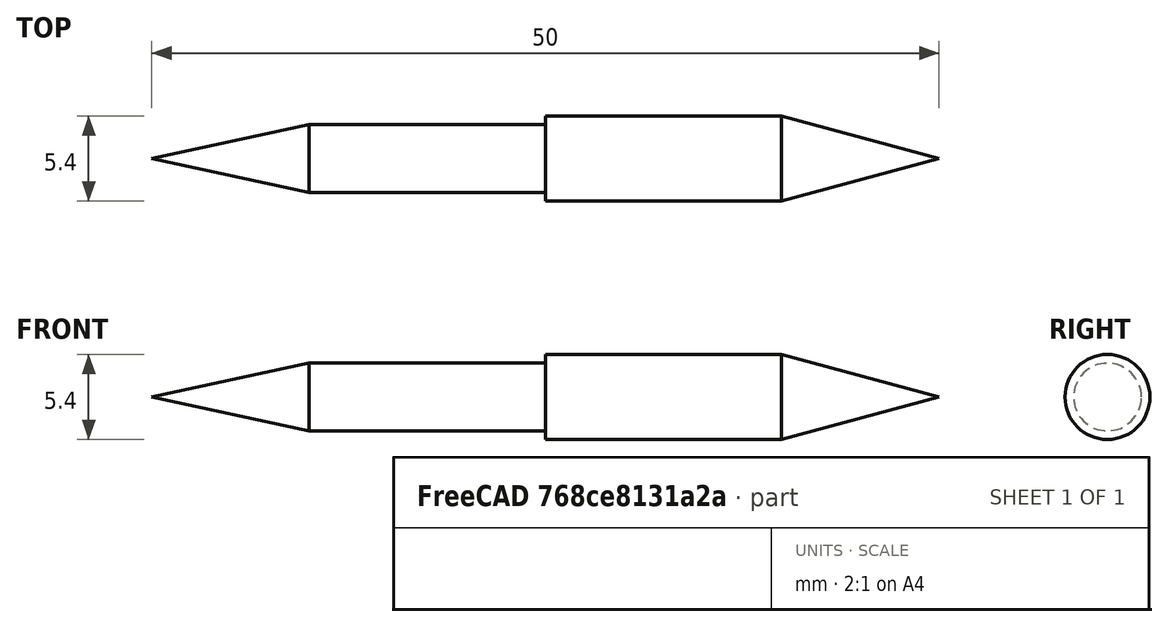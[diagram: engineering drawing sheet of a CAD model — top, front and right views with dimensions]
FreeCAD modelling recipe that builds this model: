
FCSTD DOCUMENT  (FreeCAD 1.0R38806 (Git))
Label: dowelpin
License: All rights reserved
LicenseURL: https://en.wikipedia.org/wiki/All_rights_reserved
objects: Sketcher::SketchObject×1, PartDesign::Revolution×1, PartDesign::Body×1
note: 6 computed .brp shape members not serialized (recipe doc carries the construction recipe); baked Part::Feature solids carry a one-line shape summary decoded from their .brp

FEATURE [Sketcher::SketchObject] Sketch
  ArcFitTolerance = 1e-06
  AttachmentSupport = -> [XZ_Plane]
  FullyConstrained = true
  MakeInternals = false
  MapMode = 5
  Placement = pos=(0,0,0) rot=(1,0,0;1.5708rad)
  sketch-geometry (6):
    g0: LineSegment StartX=-15 StartY=2.15 StartZ=0 EndX=0 EndY=2.15 EndZ=0
    g1: LineSegment StartX=0 StartY=2.7 StartZ=0 EndX=15 EndY=2.7 EndZ=0
    g2: LineSegment StartX=15 StartY=2.7 StartZ=0 EndX=25 EndY=0 EndZ=0
    g3: LineSegment StartX=-25 StartY=0 StartZ=0 EndX=-15 EndY=2.15 EndZ=0
    g4: LineSegment StartX=0 StartY=2.7 StartZ=0 EndX=0 EndY=2.15 EndZ=0
    g5: LineSegment StartX=-25 StartY=0 StartZ=0 EndX=25 EndY=0 EndZ=0
  constraints (18):
    c: Horizontal(g0)
    c: PointOnObject(g1,g-2)
    c: Horizontal(g1)
    c: Coincident(g2,g1)
    c: Coincident(g3,g0)
    c: Coincident(g4,g1)
    c: Coincident(g4,g0)
    c: DistanceX(g1,g1) = 15
    c: Coincident(g5,g3)
    c: PointOnObject(g5,g-1)
    c: Horizontal(g5)
    c: Distance(g5,g0) = 2.15
    c: Distance(g5,g1) = 2.7
    c: DistanceX(g0,g0) = 15
    c: PointOnObject(g0,g-2)
    c: Coincident(g5,g2)
    c: DistanceX(g3,g0) = 10
    c: DistanceX(g1,g2) = 10
FEATURE [PartDesign::Revolution] Revolution
  Angle = 360
  Angle2 = 60
  Axis = (1,0,0)
  Base = (0,0,0)
  Placement = pos=(0,0,0) rot=(1,0,0;1.5708rad)
  Profile = -> Sketch
  ReferenceAxis = -> X_Axis
  Refine = true
  Reversed = true
  Suppressed = false
  Type = 0
FEATURE [PartDesign::Body] Body
  AllowCompound = false
  Group = -> [Sketch,Revolution]
  Origin = -> Origin
  Tip = -> Revolution
